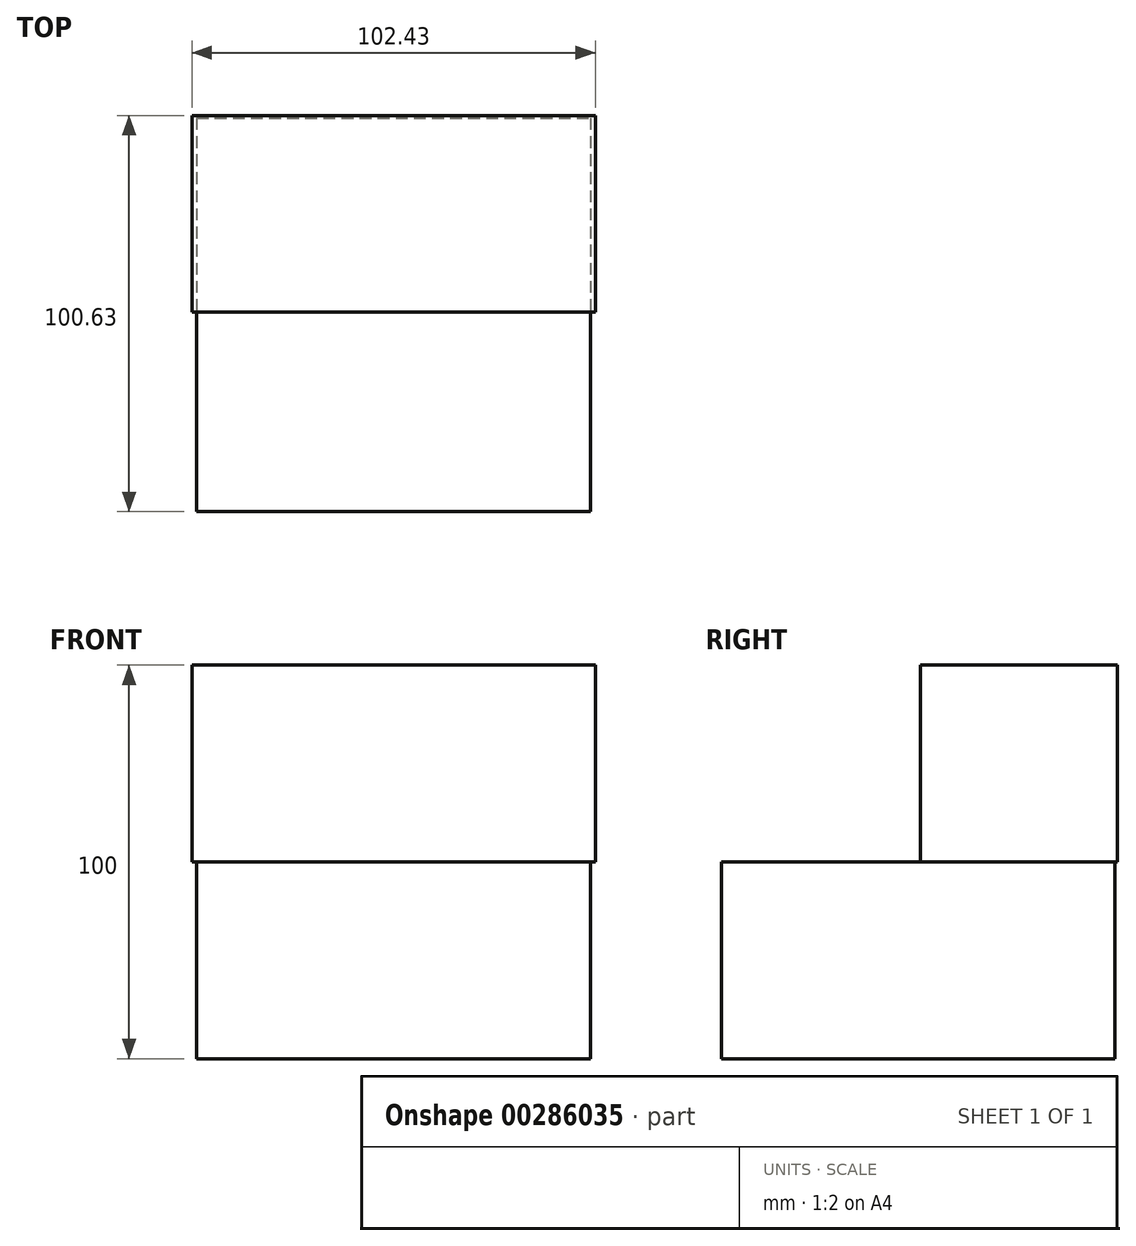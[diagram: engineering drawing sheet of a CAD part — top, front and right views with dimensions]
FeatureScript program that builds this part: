
annotation { "Feature Type Name" : "Feature", "Feature Type Description" : "" }
export const myFeature = defineFeature(function(context is Context, id is Id, definition is map)
    precondition{}
    {
        {
            var Q0;
            Q0=qCreatedBy(makeId("Top.planeOp"),FACE);
            var sketch = newSketch(context, id + "F0", { "sketchPlane" : qUnion([Q0])});
            skLineSegment(sketch, "E0.bottom", {"start": v(-45.44, 35.34) * mm, "end": v(54.56, 35.34) * mm});
            skLineSegment(sketch, "E0.top", {"start": v(-45.44, -64.66) * mm, "end": v(54.56, -64.66) * mm});
            skLineSegment(sketch, "E0.left", {"start": v(-45.44, 35.34) * mm, "end": v(-45.44, -64.66) * mm});
            skLineSegment(sketch, "E0.right", {"start": v(54.56, 35.34) * mm, "end": v(54.56, -64.66) * mm});
            skSolve(sketch);
        }
        {
            var Q0;
            Q0=makeQuery(id+"F0.imprint","IMPRINT",FACE,{"disambiguationData":[TD([[makeQuery(id+"F0.imprint","IMPRINT",EDGE,{"derivedFrom":sQuery(id+"F0.wireOp",EDGE,"E0.bottom")}),-1.0]])]});
            extrude(context, id + "F1", {"entities" : qUnion([Q0]), "oppositeDirection" : true, "depth" : 50 * mm});
        }
        {
            var Q0;
            Q0=qCreatedBy(makeId("Top.planeOp"),FACE);
            var sketch = newSketch(context, id + "F2", { "sketchPlane" : qUnion([Q0])});
            skLineSegment(sketch, "E1.bottom", {"start": v(-46.6, -14.03) * mm, "end": v(55.84, -14.03) * mm});
            skLineSegment(sketch, "E1.top", {"start": v(-46.6, 35.97) * mm, "end": v(55.84, 35.97) * mm});
            skLineSegment(sketch, "E1.left", {"start": v(-46.6, -14.03) * mm, "end": v(-46.6, 35.97) * mm});
            skLineSegment(sketch, "E1.right", {"start": v(55.84, -14.03) * mm, "end": v(55.84, 35.97) * mm});
            skSolve(sketch);
        }
        {
            var Q0;
            Q0=makeQuery(id+"F2.imprint","IMPRINT",FACE,{"disambiguationData":[TD([[makeQuery(id+"F2.imprint","IMPRINT",EDGE,{"derivedFrom":sQuery(id+"F2.wireOp",EDGE,"E1.bottom")}),1.0]])]});
            extrude(context, id + "F3", {"entities" : qUnion([Q0]), "operationType" : NewBodyOperationType.ADD, "depth" : 50 * mm});
        }
    });
